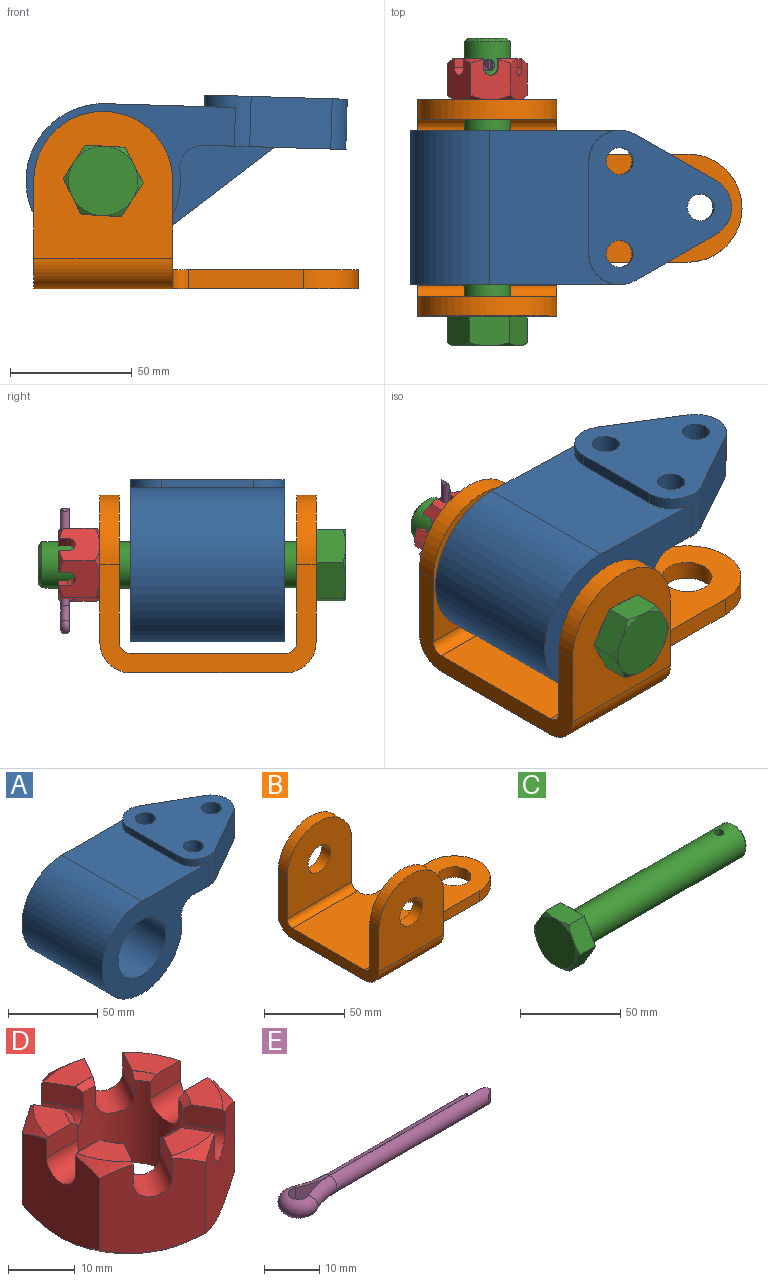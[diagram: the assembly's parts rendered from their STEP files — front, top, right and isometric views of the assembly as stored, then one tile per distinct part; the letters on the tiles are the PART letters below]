
ASSEMBLY  parts=5 mates=4
PART A: 21 faces, bbox 131.3x63.5x68.3 mm
  f0: cylinder r=31.75mm len=63.5mm, axis (0,1,0), area 9496.9mm2, adj f1,f13,f14,f16,f17,f18,f19,f20
  f1: cylinder r=9.53mm len=26.99mm, axis (0,1,0), area 443.5mm2, adj f0,f11,f17,f20
  f2: plane 33.35x20.65mm, normal (0.5,0.87,0), area 793.1mm2, adj f3,f10,f11,f12
  f3: cylinder r=12.7mm len=20.65mm, axis (0,0,1), area 231.4mm2, adj f2,f4,f11,f12,f13,f17
  f4: plane 38.1x4.78mm, normal (-1,0,0), area 181.9mm2, adj f3,f5,f12,f13
  f5: cylinder r=12.7mm len=20.65mm, axis (0,0,1), area 231.4mm2, adj f4,f6,f11,f12,f13,f16
  f6: plane 33.35x20.65mm, normal (0.5,-0.87,0), area 793.1mm2, adj f5,f10,f11,f12
  f7: cylinder r=5.56mm len=20.65mm, axis (0,0,1), area 721.7mm2, adj f11,f12
  f8: cylinder r=5.56mm len=20.65mm, axis (0,0,1), area 721.7mm2, adj f11,f12
  f9: cylinder r=5.56mm len=20.65mm, axis (0,0,1), area 721.7mm2, adj f11,f12
  f10: cylinder r=12.7mm len=22.06mm, axis (0,0,1), area 551.7mm2, adj f2,f6,f11,f12
  f11: plane 63.5x58.75mm, normal (0,0,-1), area 2102.2mm2, adj f1,f2,f3,f5,f6,f7,f8,f9
  f12: plane 63.5x58.75mm, normal (0,0,1), area 2309.8mm2, adj f2,f3,f4,f5,f6,f7,f8,f9
  f13: plane 63.5x53.48mm, normal (0,0,1), area 2659mm2, adj f0,f3,f4,f5,f16,f17
  f14: cylinder r=9.53mm len=26.99mm, axis (0,1,0), area 443.5mm2, adj f0,f11,f16,f19
  f15: cylinder r=19.05mm len=63.5mm, axis (0,1,0), area 7600.6mm2, adj f16,f17
  f16: plane 85.23x63.5mm, normal (0,-1,0), area 2601.7mm2, adj f0,f5,f11,f13,f14,f15
  f17: plane 85.23x63.5mm, normal (0,1,0), area 2601.7mm2, adj f0,f1,f3,f11,f13,f15
  f18: plane 49.82x40.51mm, normal (0.63,0,-0.78), area 611.6mm2, adj f0,f11,f19,f20
  f19: plane 49.82x40.51mm, normal (0,-1,0), area 608.6mm2, adj f0,f11,f14,f18
  f20: plane 49.82x40.51mm, normal (0,1,0), area 608.6mm2, adj f0,f1,f11,f18
PART B: 24 faces, bbox 133.4x88.9x73 mm
  f0: plane 60.33x57.15mm, normal (0,-1,0), area 2787.8mm2, adj f5,f9,f10,f12,f22
  f1: plane 133.35x63.5mm, normal (0,0,1), area 6151.6mm2, adj f5,f8,f9,f13,f14,f15,f16,f17
  f2: plane 60.33x57.15mm, normal (0,-1,0), area 2787.8mm2, adj f5,f7,f8,f11,f20
  f3: plane 60.33x57.15mm, normal (0,1,0), area 2787.8mm2, adj f5,f9,f10,f12,f21
  f4: plane 60.33x57.15mm, normal (0,1,0), area 2787.8mm2, adj f5,f7,f8,f11,f23
  f5: plane 88.9x44.45mm, normal (-1,0,0), area 1225.8mm2, adj f0,f1,f2,f3,f4,f6,f7,f10
  f6: plane 133.35x63.5mm, normal (0,0,-1), area 6151.6mm2, adj f5,f8,f9,f13,f14,f15,f16,f17
  f7: cylinder r=28.57mm len=57.15mm, axis (0,-1,0), area 712.6mm2, adj f2,f4,f5,f8
  f8: plane 44.45x15.88mm, normal (1,0,0), area 386.1mm2, adj f1,f2,f4,f6,f7,f14,f20,f23
  f9: plane 44.45x15.88mm, normal (1,0,0), area 386.1mm2, adj f0,f1,f3,f6,f10,f18,f21,f22
  f10: cylinder r=28.57mm len=57.15mm, axis (0,-1,0), area 712.6mm2, adj f0,f3,f5,f9
  f11: cylinder r=9.92mm len=19.85mm, axis (0,-1,0), area 494.9mm2, adj f2,f4
  f12: cylinder r=9.92mm len=19.85mm, axis (0,-1,0), area 494.9mm2, adj f0,f3
  f13: cylinder r=10.33mm len=20.65mm, axis (0,0,1), area 514.9mm2, adj f1,f6
  f14: cylinder r=6.35mm len=7.94mm, axis (0,0,1), area 79.2mm2, adj f1,f6,f8,f15
  f15: plane 47.63x7.94mm, normal (0,1,0), area 378mm2, adj f1,f6,f14,f16
  f16: cylinder r=22.23mm len=44.45mm, axis (0,0,1), area 554.2mm2, adj f1,f6,f15,f19
  f17: cylinder r=10.33mm len=20.65mm, axis (0,0,1), area 514.9mm2, adj f1,f6
  f18: cylinder r=6.35mm len=7.94mm, axis (0,0,1), area 79.2mm2, adj f1,f6,f9,f19
  f19: plane 47.63x7.94mm, normal (0,-1,0), area 378mm2, adj f1,f6,f16,f18
  f20: cylinder r=4.76mm len=57.15mm, axis (1,0,0), area 427.5mm2, adj f1,f2,f5,f8
  f21: cylinder r=4.76mm len=57.15mm, axis (1,0,0), area 427.5mm2, adj f1,f3,f5,f9
  f22: cylinder r=12.7mm len=57.15mm, axis (-1,0,0), area 1140.1mm2, adj f0,f5,f6,f9
  f23: cylinder r=12.7mm len=57.15mm, axis (-1,0,0), area 1140.1mm2, adj f4,f5,f6,f8
PART C: 26 faces, bbox 126.6x33x33 mm
  f0: plane 28.58x28.58mm, normal (1,0,0), area 325.1mm2, adj f10,f24
  f1: cylinder r=9.53mm len=112.28mm, axis (-1,0,0), area 6683.8mm2, adj f2,f24,f25
  f2: cone r=8.01mm half-angle=45deg, axis (-1,0,0), area 117.9mm2, adj f1,f3
  f3: plane 16.03x16.03mm, normal (1,0,0), area 201.7mm2, adj f2
  f4: plane 12.37x7.14mm, normal (1,0,0), area 11mm2, adj f10,f18,f23
  f5: plane 14.29x4.12mm, normal (1,0,0), area 11mm2, adj f10,f22,f23
  f6: plane 12.37x7.14mm, normal (1,0,0), area 11mm2, adj f10,f21,f22
  f7: plane 12.37x7.14mm, normal (1,0,0), area 11mm2, adj f10,f20,f21
  f8: plane 14.29x4.12mm, normal (1,0,0), area 11mm2, adj f10,f19,f20
  f9: plane 12.37x7.14mm, normal (1,0,0), area 11mm2, adj f10,f18,f19
  f10: cylinder r=14.29mm len=28.58mm, axis (-1,0,0), area 34.2mm2, adj f0,f4,f5,f6,f7,f8,f9
  f11: plane 28.58x28.58mm, normal (-1,0,0), area 641.3mm2, adj f12,f13,f14,f15,f16,f17
  f12: cone r=14.29mm half-angle=60deg, axis (1,0,0), area 12.7mm2, adj f11,f22,f23
  f13: cone r=14.29mm half-angle=60deg, axis (1,0,0), area 12.7mm2, adj f11,f21,f22
  f14: cone r=14.29mm half-angle=60deg, axis (1,0,0), area 12.7mm2, adj f11,f20,f21
  f15: cone r=14.29mm half-angle=60deg, axis (1,0,0), area 12.7mm2, adj f11,f19,f20
  f16: cone r=14.29mm half-angle=60deg, axis (1,0,0), area 12.7mm2, adj f11,f18,f23
  f17: cone r=14.29mm half-angle=60deg, axis (1,0,0), area 12.7mm2, adj f11,f18,f19
  f18: plane 16.51x11.89mm, normal (0,0,-1), area 188.9mm2, adj f4,f9,f16,f17,f19,f23
  f19: plane 14.29x11.89mm, normal (0,-0.87,-0.5), area 188.9mm2, adj f8,f9,f15,f17,f18,f20
  f20: plane 14.29x11.89mm, normal (0,-0.87,0.5), area 188.9mm2, adj f7,f8,f14,f15,f19,f21
  f21: plane 16.51x11.89mm, normal (0,0,1), area 188.9mm2, adj f6,f7,f13,f14,f20,f22
  f22: plane 14.29x11.89mm, normal (0,0.87,0.5), area 188.9mm2, adj f5,f6,f12,f13,f21,f23
  f23: plane 14.29x11.89mm, normal (0,0.87,-0.5), area 188.9mm2, adj f4,f5,f12,f16,f18,f22
  f24: torus R=10.03mm, axis (1,0,0), area 48.7mm2, adj f0,f1
  f25: cylinder r=2.38mm len=19.05mm, axis (0,0,1), area 285mm2, adj f1
PART D: 64 faces, bbox 33x33x16.9 mm
  f0: cylinder r=8.33mm len=16.67mm, axis (0,0,1), area 599.6mm2, adj f8,f9,f10,f11,f12,f13,f14,f15
  f1: plane 28.58x28.58mm, normal (0,0,-1), area 356.3mm2, adj f32,f33,f34,f35,f36,f37,f51
  f2: plane 8.68x4.95mm, normal (0,0,1), area 30mm2, adj f12,f16,f41,f48
  f3: plane 7.52x6.81mm, normal (0,0,1), area 30mm2, adj f9,f13,f43,f49
  f4: plane 7.52x6.81mm, normal (0,0,1), area 30mm2, adj f8,f18,f39,f44
  f5: plane 7.52x6.81mm, normal (0,0,1), area 30mm2, adj f11,f15,f42,f46
  f6: plane 7.52x6.81mm, normal (0,0,1), area 30mm2, adj f10,f17,f40,f47
  f7: plane 8.68x4.95mm, normal (0,0,1), area 30mm2, adj f14,f19,f38,f45
  f8: plane 6.56x3.71mm, normal (0,-1,0), area 23.4mm2, adj f0,f4,f22,f26,f39,f44,f62,f63
  f9: plane 6.56x3.71mm, normal (0,1,0), area 23.4mm2, adj f0,f3,f22,f26,f43,f49,f52,f53
  f10: plane 6.56x3.71mm, normal (0,1,0), area 23.4mm2, adj f0,f6,f25,f27,f40,f47,f56,f57
  f11: plane 6.56x3.71mm, normal (0,-1,0), area 23.4mm2, adj f0,f5,f25,f27,f42,f46,f58,f59
  f12: plane 5.69x3.71mm, normal (0.87,0.5,0), area 23.4mm2, adj f0,f2,f23,f28,f41,f48,f54,f55
  f13: plane 5.69x3.71mm, normal (-0.87,-0.5,0), area 23.4mm2, adj f0,f3,f23,f28,f43,f49,f52,f53
  f14: plane 5.69x3.71mm, normal (-0.87,-0.5,0), area 23.4mm2, adj f0,f7,f20,f29,f38,f45,f60,f61
  f15: plane 5.69x3.71mm, normal (0.87,0.5,0), area 23.4mm2, adj f0,f5,f20,f29,f42,f46,f58,f59
  f16: plane 5.69x3.71mm, normal (-0.87,0.5,0), area 23.4mm2, adj f0,f2,f24,f30,f41,f48,f54,f55
  f17: plane 5.69x3.71mm, normal (0.87,-0.5,0), area 23.4mm2, adj f0,f6,f24,f30,f40,f47,f56,f57
  f18: plane 5.69x3.71mm, normal (-0.87,0.5,0), area 23.4mm2, adj f0,f4,f21,f31,f39,f44,f62,f63
  f19: plane 5.69x3.71mm, normal (0.87,-0.5,0), area 23.4mm2, adj f0,f7,f21,f31,f38,f45,f60,f61
  f20: plane 16.62x14.29mm, normal (-0.5,0.87,0), area 220.6mm2, adj f14,f15,f21,f25,f29,f32,f33,f38
  f21: plane 16.62x14.29mm, normal (0.5,0.87,0), area 220.6mm2, adj f18,f19,f20,f22,f31,f33,f34,f38
  f22: plane 16.63x16.51mm, normal (1,0,0), area 220.6mm2, adj f8,f9,f21,f23,f26,f34,f35,f39
  f23: plane 16.62x14.29mm, normal (0.5,-0.87,0), area 220.6mm2, adj f12,f13,f22,f24,f28,f35,f36,f41
  f24: plane 16.62x14.29mm, normal (-0.5,-0.87,0), area 220.6mm2, adj f16,f17,f23,f25,f30,f36,f37,f40
  f25: plane 16.63x16.51mm, normal (-1,0,0), area 220.6mm2, adj f10,f11,f20,f24,f27,f32,f37,f40
  f26: cylinder r=3.05mm len=6.53mm, axis (1,0,0), area 59.8mm2, adj f0,f8,f9,f22
  f27: cylinder r=3.05mm len=6.53mm, axis (1,0,0), area 59.8mm2, adj f0,f10,f11,f25
  f28: cylinder r=3.05mm len=8.7mm, axis (-0.5,0.87,0), area 59.8mm2, adj f0,f12,f13,f23
  f29: cylinder r=3.05mm len=8.7mm, axis (-0.5,0.87,0), area 59.8mm2, adj f0,f14,f15,f20
  f30: cylinder r=3.05mm len=8.7mm, axis (0.5,0.87,0), area 59.8mm2, adj f0,f16,f17,f24
  f31: cylinder r=3.05mm len=8.7mm, axis (0.5,0.87,0), area 59.8mm2, adj f0,f18,f19,f21
  f32: cone r=14.29mm half-angle=49.2deg, axis (0,0,1), area 14.5mm2, adj f1,f20,f25
  f33: cone r=14.29mm half-angle=49.2deg, axis (0,0,1), area 14.5mm2, adj f1,f20,f21
  f34: cone r=14.29mm half-angle=49.2deg, axis (0,0,1), area 14.5mm2, adj f1,f21,f22
  f35: cone r=14.29mm half-angle=49.2deg, axis (0,0,1), area 14.5mm2, adj f1,f22,f23
  f36: cone r=14.29mm half-angle=49.2deg, axis (0,0,1), area 14.5mm2, adj f1,f23,f24
  f37: cone r=14.29mm half-angle=49.2deg, axis (0,0,1), area 14.5mm2, adj f1,f24,f25
  f38: cone r=14.29mm half-angle=49.2deg, axis (0,0,-1), area 13.6mm2, adj f7,f14,f19,f20,f21
  f39: cone r=14.29mm half-angle=49.2deg, axis (0,0,-1), area 13.6mm2, adj f4,f8,f18,f21,f22
  f40: cone r=14.29mm half-angle=49.2deg, axis (0,0,-1), area 13.6mm2, adj f6,f10,f17,f24,f25
  f41: cone r=14.29mm half-angle=49.2deg, axis (0,0,-1), area 13.6mm2, adj f2,f12,f16,f23,f24
  f42: cone r=14.29mm half-angle=49.2deg, axis (0,0,-1), area 13.6mm2, adj f5,f11,f15,f20,f25
  f43: cone r=14.29mm half-angle=49.2deg, axis (0,0,-1), area 13.6mm2, adj f3,f9,f13,f22,f23
  f44: cone r=8.21mm half-angle=55deg, axis (0,0,1), area 0.1mm2, adj f4,f8,f18,f63
  f45: cone r=8.21mm half-angle=55deg, axis (0,0,1), area 0.1mm2, adj f7,f14,f19,f60
  f46: cone r=8.21mm half-angle=55deg, axis (0,0,1), area 0.1mm2, adj f5,f11,f15,f58
  f47: cone r=8.21mm half-angle=55deg, axis (0,0,1), area 0.1mm2, adj f6,f10,f17,f56
  f48: cone r=8.21mm half-angle=55deg, axis (0,0,1), area 0.1mm2, adj f2,f12,f16,f54
  f49: cone r=8.21mm half-angle=55deg, axis (0,0,1), area 0.1mm2, adj f3,f9,f13,f52
  f50: cone r=9.53mm half-angle=55deg, axis (0,0,-1), area 81.6mm2, adj f0,f51
  f51: cylinder r=9.53mm len=19.05mm, axis (0,0,1), area 1.5mm2, adj f1,f50
  f52: cone r=9.53mm half-angle=55deg, axis (0,0,-1), area 0.1mm2, adj f9,f13,f49,f53
  f53: cone r=8.33mm half-angle=55deg, axis (0,0,1), area 4.5mm2, adj f0,f9,f13,f52
  f54: cone r=9.53mm half-angle=55deg, axis (0,0,-1), area 0.1mm2, adj f12,f16,f48,f55
  f55: cone r=8.33mm half-angle=55deg, axis (0,0,1), area 4.5mm2, adj f0,f12,f16,f54
  f56: cone r=9.53mm half-angle=55deg, axis (0,0,-1), area 0.1mm2, adj f10,f17,f47,f57
  f57: cone r=8.33mm half-angle=55deg, axis (0,0,1), area 4.5mm2, adj f0,f10,f17,f56
  f58: cone r=9.53mm half-angle=55deg, axis (0,0,-1), area 0.1mm2, adj f11,f15,f46,f59
  f59: cone r=8.33mm half-angle=55deg, axis (0,0,1), area 4.5mm2, adj f0,f11,f15,f58
  f60: cone r=9.53mm half-angle=55deg, axis (0,0,-1), area 0.1mm2, adj f14,f19,f45,f61
  f61: cone r=8.33mm half-angle=55deg, axis (0,0,1), area 4.5mm2, adj f0,f14,f19,f60
  f62: cone r=8.33mm half-angle=55deg, axis (0,0,1), area 4.5mm2, adj f0,f8,f18,f63
  f63: cone r=9.53mm half-angle=55deg, axis (0,0,-1), area 0.1mm2, adj f8,f18,f44,f62
PART E: 14 faces, bbox 52x8x3.7 mm
  f0: plane 38.67x3.7mm, normal (0,1,0), area 143.1mm2, adj f1,f2,f13
  f1: cylinder r=1.85mm len=40mm, axis (1,0,0), area 227.7mm2, adj f0,f3,f12,f13
  f2: cylinder r=16.37mm len=7.19mm, axis (0,0,-1), area 27.5mm2, adj f0,f3,f4
  f3: torus R=16.37mm, axis (0,0,-1), area 40.1mm2, adj f1,f2,f5
  f4: cylinder r=1.85mm len=3.7mm, axis (0,0,1), area 27.8mm2, adj f2,f5,f6
  f5: torus R=1.85mm, axis (0,0,1), area 71.2mm2, adj f3,f4,f7
  f6: cylinder r=16.37mm len=7.19mm, axis (0,0,-1), area 27.5mm2, adj f4,f7,f9
  f7: torus R=16.37mm, axis (0,0,-1), area 40.1mm2, adj f5,f6,f8
  f8: cylinder r=1.85mm len=36mm, axis (1,0,0), area 204.5mm2, adj f7,f9,f10,f11
  f9: plane 34.67x3.7mm, normal (0,-1,0), area 128.3mm2, adj f6,f8,f10
  f10: plane 3.7x1.33mm, normal (0.57,-0.82,0), area 5.7mm2, adj f8,f9,f11
  f11: plane 3.2x1.31mm, normal (0.58,0.82,0), area 3.6mm2, adj f8,f10
  f12: plane 3.2x1.31mm, normal (0.58,-0.82,0), area 3.6mm2, adj f1,f13
  f13: plane 3.7x1.33mm, normal (0.57,0.82,0), area 5.7mm2, adj f0,f1,f12
PLACE A rot(axis=(0,1,0),1.7deg) t=(58.68,44.93,70.37)mm
PLACE B t=(-11.74,44.78,-9.38)mm fixed
PLACE C rot(axis=(-0.71,-0.71,0.02),177.7deg) t=(16.83,-11.94,35.07)mm
PLACE D rot(axis=(-0.22,-0.69,-0.69),154.9deg) t=(16.83,106.1,35.07)mm
PLACE E rot(axis=(-0.6,-0.57,-0.57),118.1deg) t=(15.42,103.52,10.4)mm
MATE revolute C.f1 <-> B.f7  axis (0,1,0) through (16.83,0.33,35.07)mm
MATE slider E.f8 <-> C.f25  axis (0.06,0,1) through (15.87,103.52,18.38)mm
MATE revolute D.f0 <-> B.f7  axis (0,1,0) through (16.83,89.23,35.07)mm
MATE cylindrical A.f0 <-> C.f1  axis (0,1,0) through (16.83,44.93,35.07)mm
